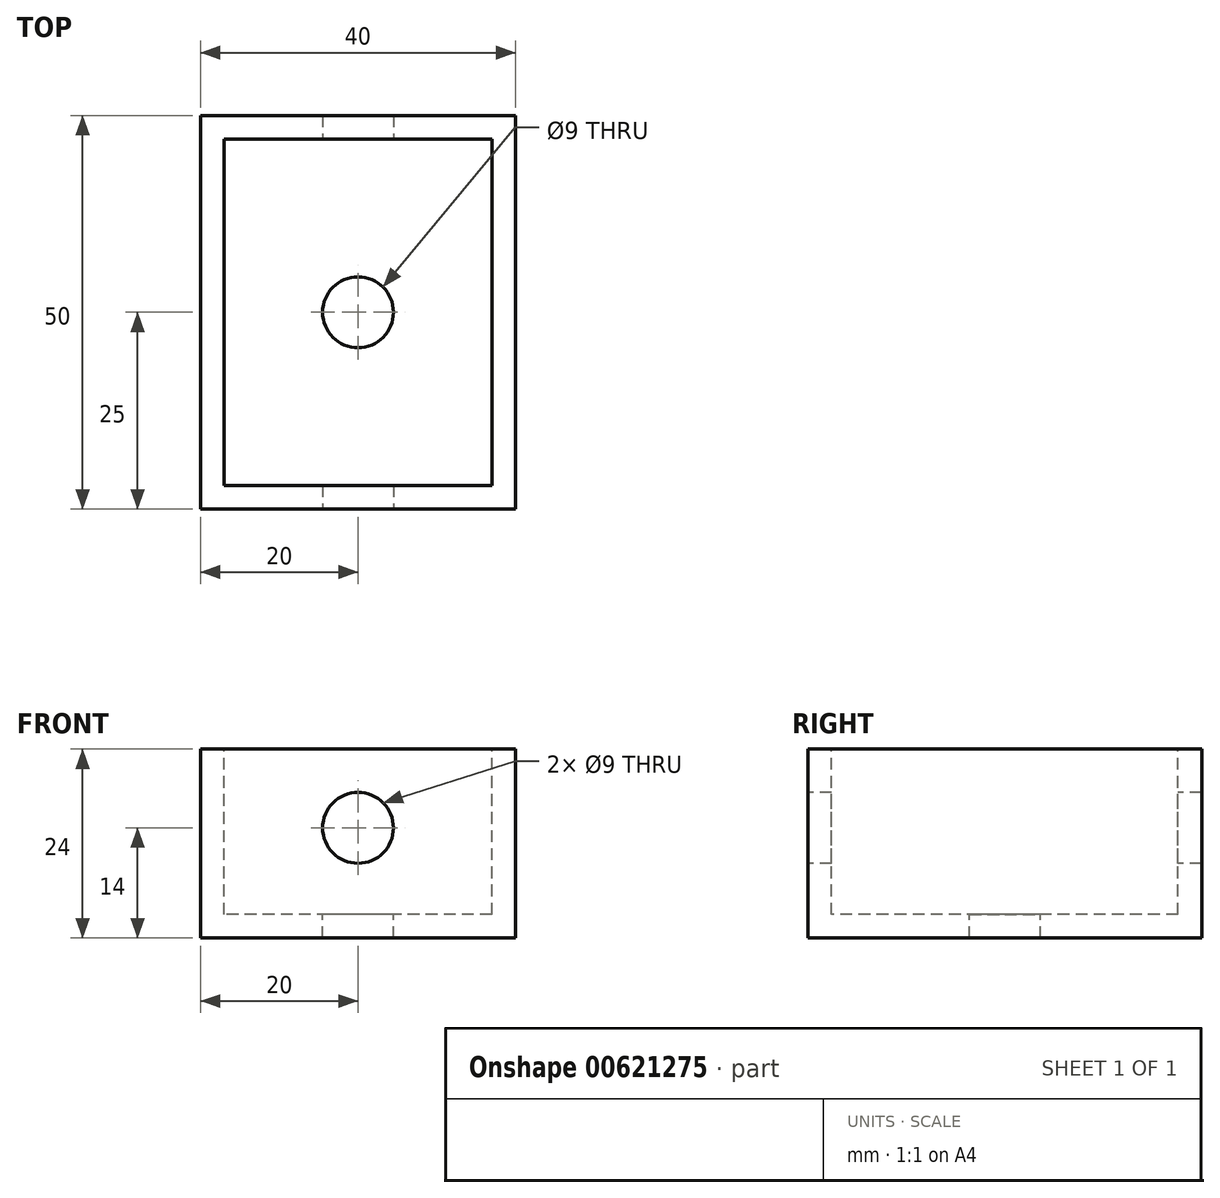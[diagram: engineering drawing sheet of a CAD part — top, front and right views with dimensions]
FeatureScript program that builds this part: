
annotation { "Feature Type Name" : "Feature", "Feature Type Description" : "" }
export const myFeature = defineFeature(function(context is Context, id is Id, definition is map)
    precondition{}
    {
        {
            var Q0;
            Q0=qCreatedBy(makeId("Top.planeOp"),FACE);
            var sketch = newSketch(context, id + "F0", { "sketchPlane" : qUnion([Q0])});
            skLineSegment(sketch, "E0.bottom", {"start": v(20, 25) * mm, "end": v(-20, 25) * mm});
            skLineSegment(sketch, "E0.top", {"start": v(20, -25) * mm, "end": v(-20, -25) * mm});
            skLineSegment(sketch, "E0.left", {"start": v(20, 25) * mm, "end": v(20, -25) * mm});
            skLineSegment(sketch, "E0.right", {"start": v(-20, 25) * mm, "end": v(-20, -25) * mm});
            skPoint(sketch, "E0.middle", {"position": v(0, 0) * mm});
            skSolve(sketch);
        }
        {
            var Q0;
            Q0=makeQuery(id+"F0.imprint","IMPRINT",FACE,{"disambiguationData":[TD([[makeQuery(id+"F0.imprint","IMPRINT",EDGE,{"derivedFrom":sQuery(id+"F0.wireOp",EDGE,"E0.bottom")}),1.0]])]});
            extrude(context, id + "F1", {"entities" : qUnion([Q0]), "depth" : 24 * mm, "offsetDistance" : 25 * mm});
        }
        {
            var Q0;
            Q0=makeQuery(id+"F1.opExtrude","CAP_FACE",FACE,{"disambiguationData":[OSD([sQuery(id+"F0.wireOp",EDGE,"E0.bottom"),sQuery(id+"F0.wireOp",EDGE,"E0.top"),sQuery(id+"F0.wireOp",EDGE,"E0.left"),sQuery(id+"F0.wireOp",EDGE,"E0.right")])],"isStart":false});
            var sketch = newSketch(context, id + "F2", { "sketchPlane" : qUnion([Q0])});
            skLineSegment(sketch, "E1.bottom", {"start": v(-17, -22) * mm, "end": v(17, -22) * mm});
            skLineSegment(sketch, "E1.top", {"start": v(-17, 22) * mm, "end": v(17, 22) * mm});
            skLineSegment(sketch, "E1.left", {"start": v(-17, -22) * mm, "end": v(-17, 22) * mm});
            skLineSegment(sketch, "E1.right", {"start": v(17, -22) * mm, "end": v(17, 22) * mm});
            skPoint(sketch, "E1.middle", {"position": v(0, 0) * mm});
            skSolve(sketch);
        }
        {
            var Q0;
            Q0 = qSketchRegion(id + "F2", true);
            var Q1;
            Q1=makeQuery(id+"F1.opExtrude","CAP_FACE",FACE,{"disambiguationData":[OSD([sQuery(id+"F0.wireOp",EDGE,"E0.bottom"),sQuery(id+"F0.wireOp",EDGE,"E0.top"),sQuery(id+"F0.wireOp",EDGE,"E0.left"),sQuery(id+"F0.wireOp",EDGE,"E0.right")])],"isStart":true});
            extrude(context, id + "F3", {"entities" : qUnion([Q0]), "operationType" : NewBodyOperationType.REMOVE, "endBound" : BoundingType.UP_TO_SURFACE, "oppositeDirection" : true, "depth" : 25 * mm, "endBoundEntityFace" : qUnion([Q1]), "hasOffset" : true, "offsetDistance" : 3 * mm});
        }
        {
            var Q0;
            Q0=makeQuery(id+"F1.opExtrude","SWEPT_FACE",FACE,{"disambiguationData":[OSD([sQuery(id+"F0.wireOp",EDGE,"E0.top")])]});
            var sketch = newSketch(context, id + "F4", { "sketchPlane" : qUnion([Q0])});
            skCircle(sketch, "E2", {"center": v(0, 14) * mm, "radius": 4.5 * mm});
            skSolve(sketch);
        }
        {
            var Q0;
            Q0 = qSketchRegion(id + "F4", true);
            extrude(context, id + "F5", {"entities" : qUnion([Q0]), "operationType" : NewBodyOperationType.REMOVE, "endBound" : BoundingType.THROUGH_ALL, "oppositeDirection" : true, "depth" : 25 * mm, "offsetDistance" : 25 * mm});
        }
        {
            var Q0;
            Q0=makeQuery(id+"F3.boolean.opBoolean","COPY",FACE,{"derivedFrom":makeQuery(id+"F3.opExtrude","CAP_FACE",FACE,{"disambiguationData":[OSD([sQuery(id+"F2.wireOp",EDGE,"E1.bottom"),sQuery(id+"F2.wireOp",EDGE,"E1.top"),sQuery(id+"F2.wireOp",EDGE,"E1.left"),sQuery(id+"F2.wireOp",EDGE,"E1.right")])],"isStart":false})});
            var sketch = newSketch(context, id + "F6", { "sketchPlane" : qUnion([Q0])});
            skCircle(sketch, "E3", {"center": v(0, 0) * mm, "radius": 4.5 * mm});
            skSolve(sketch);
        }
        {
            var Q0;
            Q0 = qSketchRegion(id + "F6", true);
            extrude(context, id + "F7", {"entities" : qUnion([Q0]), "operationType" : NewBodyOperationType.REMOVE, "endBound" : BoundingType.THROUGH_ALL, "oppositeDirection" : true, "depth" : 25 * mm, "offsetDistance" : 25 * mm});
        }
    });
